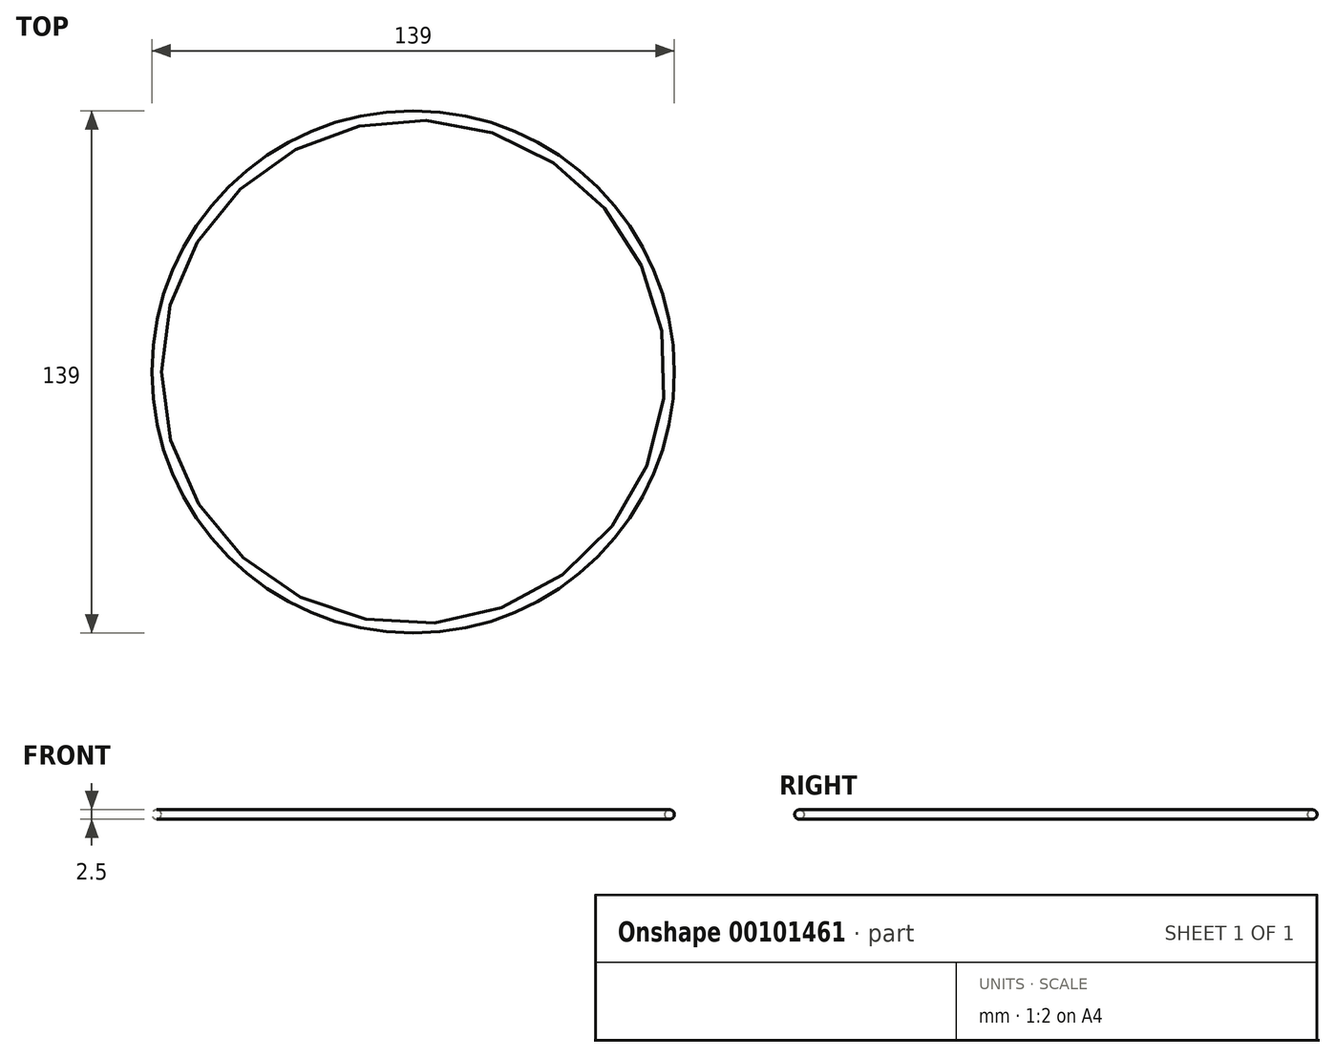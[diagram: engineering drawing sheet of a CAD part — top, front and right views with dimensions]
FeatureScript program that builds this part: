
annotation { "Feature Type Name" : "Feature", "Feature Type Description" : "" }
export const myFeature = defineFeature(function(context is Context, id is Id, definition is map)
    precondition{}
    {
        {
            var Q0;
            Q0=qCreatedBy(makeId("Top.planeOp"),FACE);
            var sketch = newSketch(context, id + "F0", { "sketchPlane" : qUnion([Q0])});
            skCircle(sketch, "E0", {"center": v(0, 0) * mm, "radius": 69.5 * mm});
            skSolve(sketch);
        }
        {
            var Q0;
            Q0=qCreatedBy(makeId("Front.planeOp"),FACE);
            var sketch = newSketch(context, id + "F1", { "sketchPlane" : qUnion([Q0])});
            skCircle(sketch, "E1", {"center": v(68.25, 0) * mm, "radius": 1.25 * mm});
            skSolve(sketch);
        }
        {
            var Q0;
            Q0 = qSketchRegion(id + "F1", true);
            var Q1;
            Q1=sQuery(id+"F0.wireOp",EDGE,"E0");
            revolve(context, id + "F2", {"entities" : qUnion([Q0]), "axis" : qUnion([Q1]), "revolveType" : RevolveType.FULL});
        }
    });
